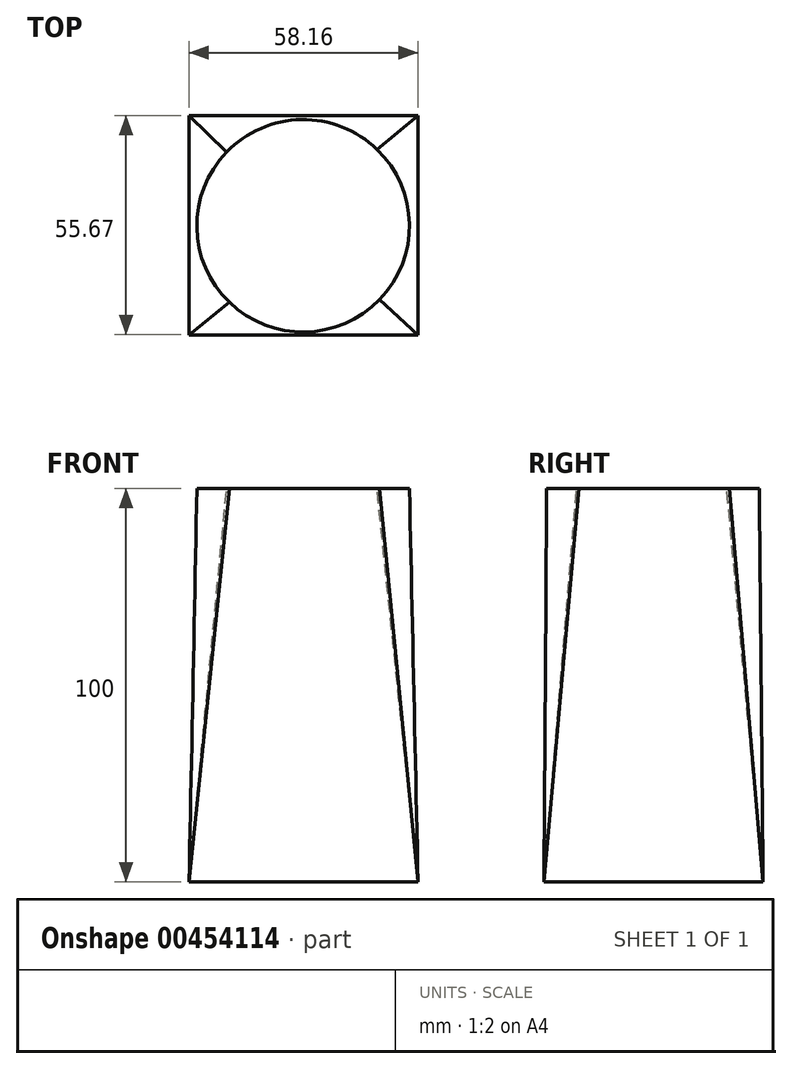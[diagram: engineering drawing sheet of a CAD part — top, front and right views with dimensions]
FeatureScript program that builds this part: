
annotation { "Feature Type Name" : "Feature", "Feature Type Description" : "" }
export const myFeature = defineFeature(function(context is Context, id is Id, definition is map)
    precondition{}
    {
        {
            var Q0;
            Q0=qCreatedBy(makeId("Top.planeOp"),FACE);
            var sketch = newSketch(context, id + "F0", { "sketchPlane" : qUnion([Q0])});
            skLineSegment(sketch, "E0.bottom", {"start": v(0, 0) * mm, "end": v(58.16, 0) * mm});
            skLineSegment(sketch, "E0.top", {"start": v(0, -55.67) * mm, "end": v(58.16, -55.67) * mm});
            skLineSegment(sketch, "E0.left", {"start": v(0, 0) * mm, "end": v(0, -55.67) * mm});
            skLineSegment(sketch, "E0.right", {"start": v(58.16, 0) * mm, "end": v(58.16, -55.67) * mm});
            skSolve(sketch);
        }
        {
            var Q0;
            Q0=qCreatedBy(makeId("Top.planeOp"),FACE);
            cPlane(context, id + "F1", {"entities" : qUnion([Q0]), "cplaneType" : CPlaneType.OFFSET, "offset" : 100 * mm, "width" : 150 * mm, "height" : 150 * mm});
        }
        {
            var Q0;
            Q0=qCreatedBy(id+"F1.planeOp",FACE);
            var sketch = newSketch(context, id + "F2", { "sketchPlane" : qUnion([Q0])});
            skCircle(sketch, "E1", {"center": v(28.97, -28) * mm, "radius": 27 * mm});
            skSolve(sketch);
        }
        {
            var Q0;
            Q0 = qSketchRegion(id + "F0", true);
            var Q1;
            Q1 = qSketchRegion(id + "F2", true);
            loft(context, id + "F3", {"sheetProfilesArray" : [{ "sheetProfileEntities" : qUnion([Q0]) }, { "sheetProfileEntities" : qUnion([Q1]) }]});
        }
    });
